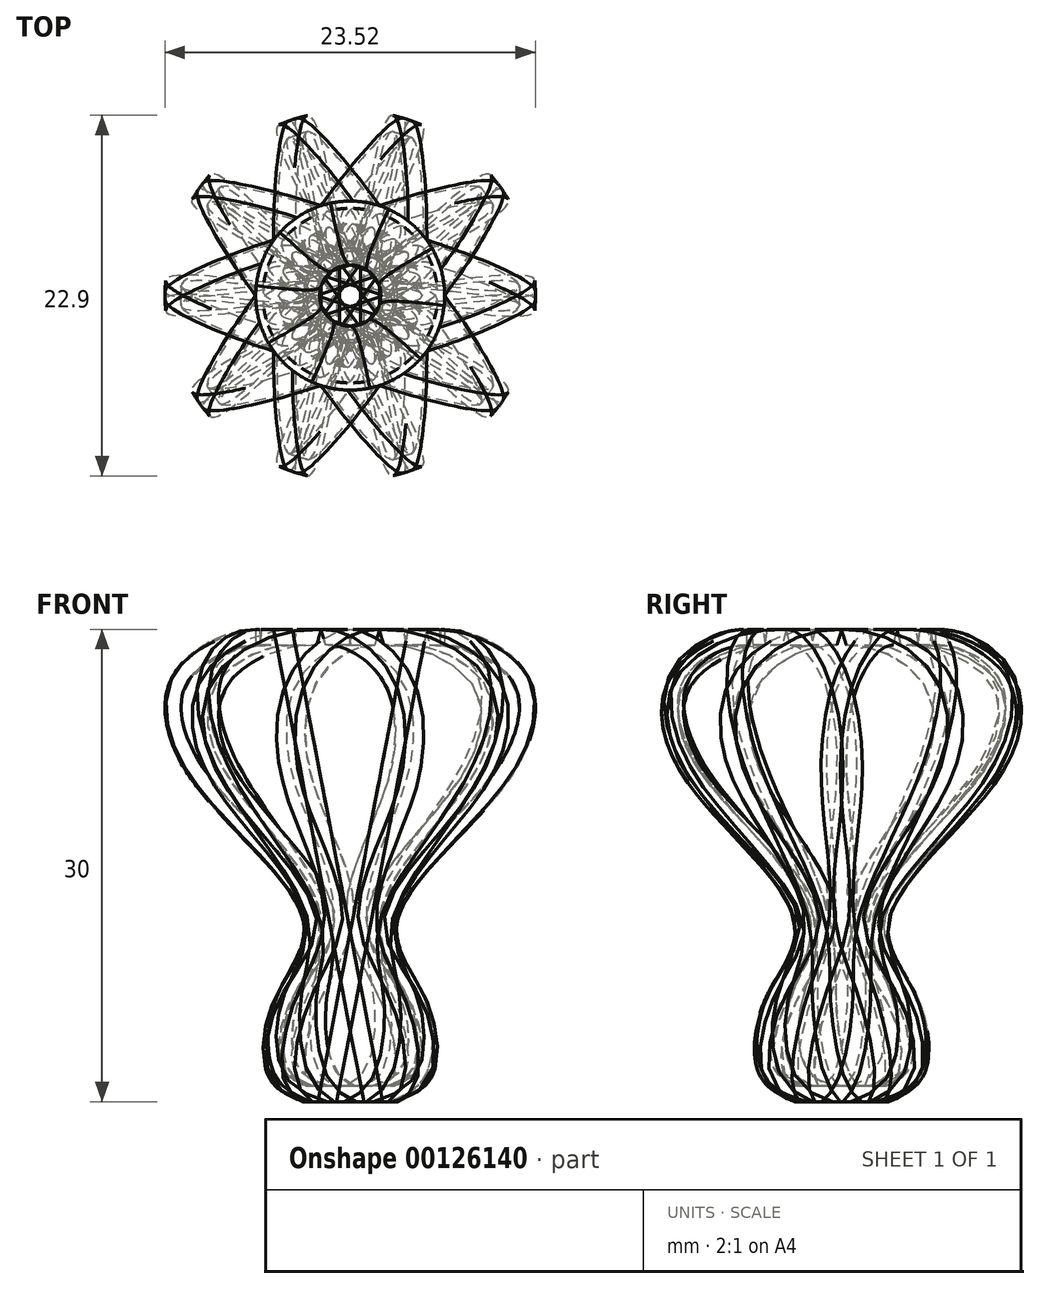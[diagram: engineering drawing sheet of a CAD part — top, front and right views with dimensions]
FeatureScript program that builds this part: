
annotation { "Feature Type Name" : "Feature", "Feature Type Description" : "" }
export const myFeature = defineFeature(function(context is Context, id is Id, definition is map)
    precondition{}
    {
        {
            assignVariable(context, id + "F0", {"name" : "Total_Height", "anyValue" : 30});
        }
        {
            var Q0;
            Q0=qCreatedBy(makeId("Top.planeOp"),FACE);
            var sketch = newSketch(context, id + "F1", { "sketchPlane" : qUnion([Q0])});
            skCircle(sketch, "E0", {"center": v(0, 0) * mm, "radius": 3 * mm});
            skSolve(sketch);
        }
        {
            var Q0;
            Q0=qCreatedBy(makeId("Top.planeOp"),FACE);
            cPlane(context, id + "F2", {"entities" : qUnion([Q0]), "cplaneType" : CPlaneType.OFFSET, "offset" : (getVariable(context, 'Total_Height')) * mm, "width" : 150 * mm, "height" : 150 * mm});
        }
        {
            var Q0;
            Q0=qCreatedBy(makeId("Front.planeOp"),FACE);
            var sketch = newSketch(context, id + "F3", { "sketchPlane" : qUnion([Q0])});
            skLineSegment(sketch, "E1", {"start": v(0, 0) * mm, "end": v(0, 30) * mm});
            skSolve(sketch);
        }
        {
            var Q0;
            Q0=qCreatedBy(id+"F2.planeOp",FACE);
            var sketch = newSketch(context, id + "F4", { "sketchPlane" : qUnion([Q0])});
            skCircle(sketch, "E2", {"center": v(0, 0) * mm, "radius": 6 * mm});
            skSolve(sketch);
        }
        {
            var Q0;
            Q0=qCreatedBy(makeId("Front.planeOp"),FACE);
            var sketch = newSketch(context, id + "F5", { "sketchPlane" : qUnion([Q0])});
            skPoint(sketch, "E3.0", {"position": v(0, 30) * mm});
            skLineSegment(sketch, "E4", {"start": v(6, 30) * mm, "end": v(0, 30) * mm});
            skLineSegment(sketch, "E5", {"start": v(3, 0) * mm, "end": v(0, 0) * mm});
            skFitSpline(sketch, "E6", {"points": [v(3, 0) * mm, v(5.17, 1.56) * mm, v(4.86, 6.5) * mm, v(3, 11.49) * mm, v(10.03, 20.39) * mm, v(11.58, 26.32) * mm, v(9.4, 28.94) * mm, v(6, 30) * mm], "startDerivative": vector(24.74, 10.04) * mm, "endDerivative": vector(-32.9, 0) * mm});
            skPoint(sketch, "E7.end.orphan", {"position": v(-6, 30) * mm});
            skPoint(sketch, "E8.end.orphan", {"position": v(-3, 0) * mm});
            skLineSegment(sketch, "E9", {"start": v(0, 30) * mm, "end": v(0, 0) * mm});
            skSolve(sketch);
        }
        {
            var Q0;
            Q0=makeQuery(id+"F5.imprint","IMPRINT",FACE,{"disambiguationData":[TD([[makeQuery(id+"F5.imprint","IMPRINT",EDGE,{"derivedFrom":sQuery(id+"F5.wireOp",EDGE,"E4")}),1.0]])]});
            var Q1;
            Q1=sQuery(id+"F5.wireOp",EDGE,"E9");
            revolve(context, id + "F6", {"entities" : qUnion([Q0]), "axis" : qUnion([Q1]), "revolveType" : RevolveType.FULL});
        }
        {
            var Q0;
            Q0=makeQuery(id+"F6.opRevolve","SWEPT_FACE",FACE,{"disambiguationData":[OSD([sQuery(id+"F5.wireOp",EDGE,"E4")])]});
            shell(context, id + "F7", {"entities" : qUnion([Q0]), "thickness" : 1 * mm});
        }
        {
            var Q0;
            Q0=qCreatedBy(makeId("Front.planeOp"),FACE);
            var sketch = newSketch(context, id + "F8", { "sketchPlane" : qUnion([Q0])});
            skLineSegment(sketch, "E10", {"start": v(-4.86, 30) * mm, "end": v(0.86, 0) * mm});
            skLineSegment(sketch, "E11", {"start": v(-3.67, 30) * mm, "end": v(2.05, 0) * mm});
            skLineSegment(sketch, "E12", {"start": v(-4.86, 30) * mm, "end": v(-3.67, 30) * mm});
            skLineSegment(sketch, "E13", {"start": v(2.05, 0) * mm, "end": v(0.86, 0) * mm});
            skSolve(sketch);
        }
        {
            var Q0;
            Q0 = qSketchRegion(id + "F8", true);
            extrude(context, id + "F9", {"entities" : qUnion([Q0]), "operationType" : NewBodyOperationType.INTERSECT, "endBound" : BoundingType.SYMMETRIC, "depth" : 25 * mm});
        }
        {
            var Q0;
            Q0=makeQuery(id+"F6.opRevolve","SWEPT_BODY",BODY,{"disambiguationData":[OSD([sQuery(id+"F5.wireOp",EDGE,"E4"),sQuery(id+"F5.wireOp",EDGE,"E5"),sQuery(id+"F5.wireOp",EDGE,"E6"),sQuery(id+"F5.wireOp",EDGE,"E9")])]});
            var Q1;
            Q1=sQuery(id+"F3.wireOp",EDGE,"E1");
            circularPattern(context, id + "F10", {"entities" : qUnion([Q0]), "axis" : qUnion([Q1]), "angle" : 360 * degree, "instanceCount" : 10, "equalSpace" : true});
        }
    });
